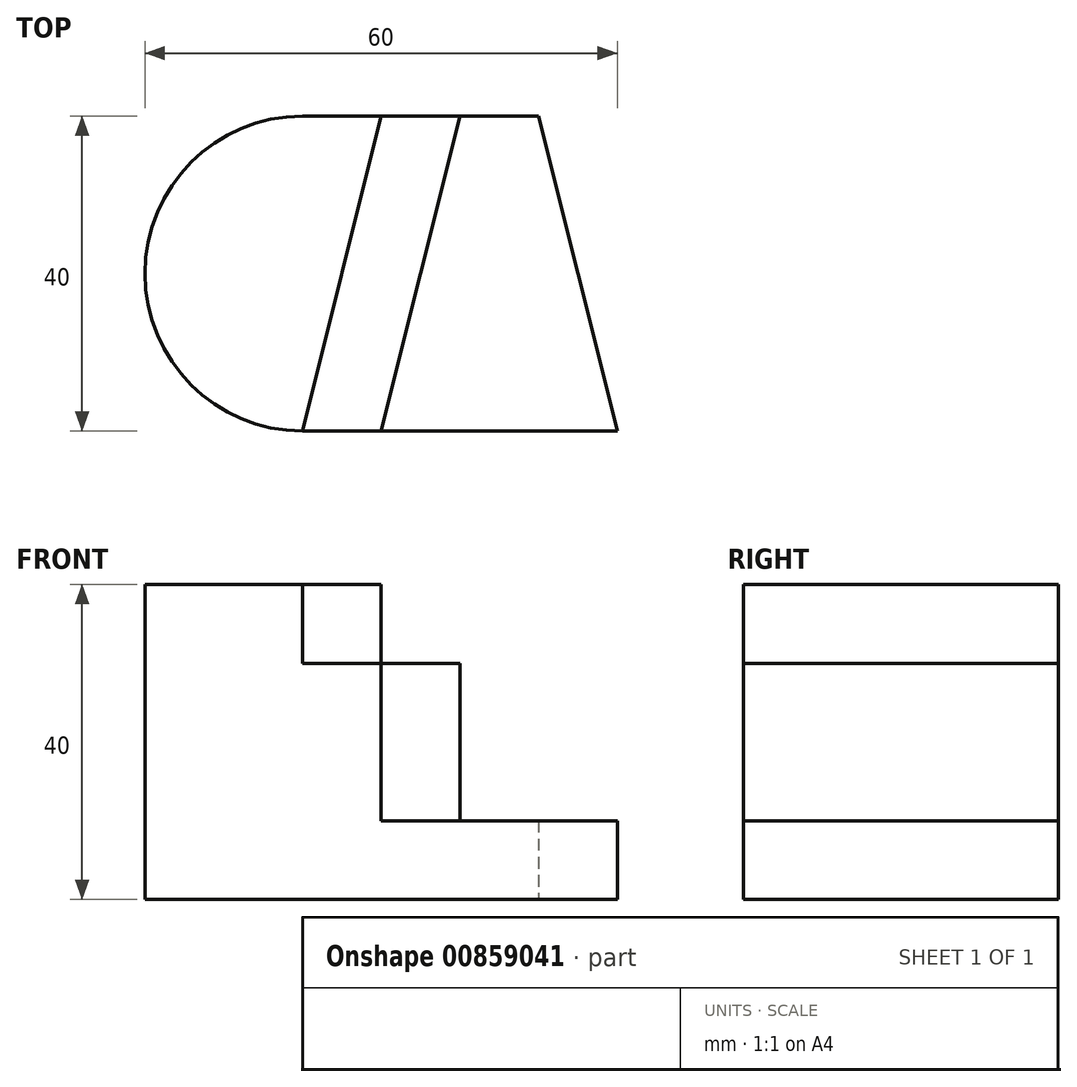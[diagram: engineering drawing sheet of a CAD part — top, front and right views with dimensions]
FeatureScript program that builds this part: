
annotation { "Feature Type Name" : "Feature", "Feature Type Description" : "" }
export const myFeature = defineFeature(function(context is Context, id is Id, definition is map)
    precondition{}
    {
        {
            var Q0;
            Q0=qCreatedBy(makeId("Top.planeOp"),FACE);
            var sketch = newSketch(context, id + "F0", { "sketchPlane" : qUnion([Q0])});
            skArc(sketch, "E0", {"start": v(0, 20) * mm, "mid": v(-20, 0) * mm, "end": v(0, -20) * mm});
            skLineSegment(sketch, "E1", {"start": v(0, -20) * mm, "end": v(40, -20) * mm});
            skLineSegment(sketch, "E2", {"start": v(0, 20) * mm, "end": v(30, 20) * mm});
            skLineSegment(sketch, "E3", {"start": v(30, 20) * mm, "end": v(40, -20) * mm});
            skLineSegment(sketch, "E4", {"start": v(-20, 0) * mm, "end": v(-20, -20) * mm, "construction": true});
            skLineSegment(sketch, "E5", {"start": v(0, -20) * mm, "end": v(10, 20) * mm});
            skLineSegment(sketch, "E6", {"start": v(10, -20) * mm, "end": v(20, 20) * mm});
            skSolve(sketch);
        }
        {
            var Q0;
            {var subQ0=sQuery(id+"F0.wireOp",EDGE,"E3");Q0=makeQuery(id+"F0.imprint","IMPRINT",FACE,{"disambiguationData":[TD([[makeQuery(id+"F0.imprint","IMPRINT",EDGE,{"derivedFrom":subQ0}),-1.0]])]});}
            extrude(context, id + "F1", {"entities" : qUnion([Q0]), "depth" : 10 * mm, "offsetDistance" : 25 * mm});
        }
        {
            var Q0;
            {var subQ0=sQuery(id+"F0.wireOp",EDGE,"E5");Q0=makeQuery(id+"F0.imprint","IMPRINT",FACE,{"disambiguationData":[TD([[makeQuery(id+"F0.imprint","IMPRINT",EDGE,{"derivedFrom":subQ0}),-1.0]])]});}
            extrude(context, id + "F2", {"entities" : qUnion([Q0]), "operationType" : NewBodyOperationType.ADD, "depth" : 30 * mm, "offsetDistance" : 25 * mm});
        }
        {
            var Q0;
            {var subQ0=sQuery(id+"F0.wireOp",EDGE,"E0");Q0=makeQuery(id+"F0.imprint","IMPRINT",FACE,{"disambiguationData":[TD([[makeQuery(id+"F0.imprint","IMPRINT",EDGE,{"derivedFrom":subQ0}),1.0]])]});}
            extrude(context, id + "F3", {"entities" : qUnion([Q0]), "operationType" : NewBodyOperationType.ADD, "depth" : 40 * mm, "offsetDistance" : 25 * mm});
        }
    });
